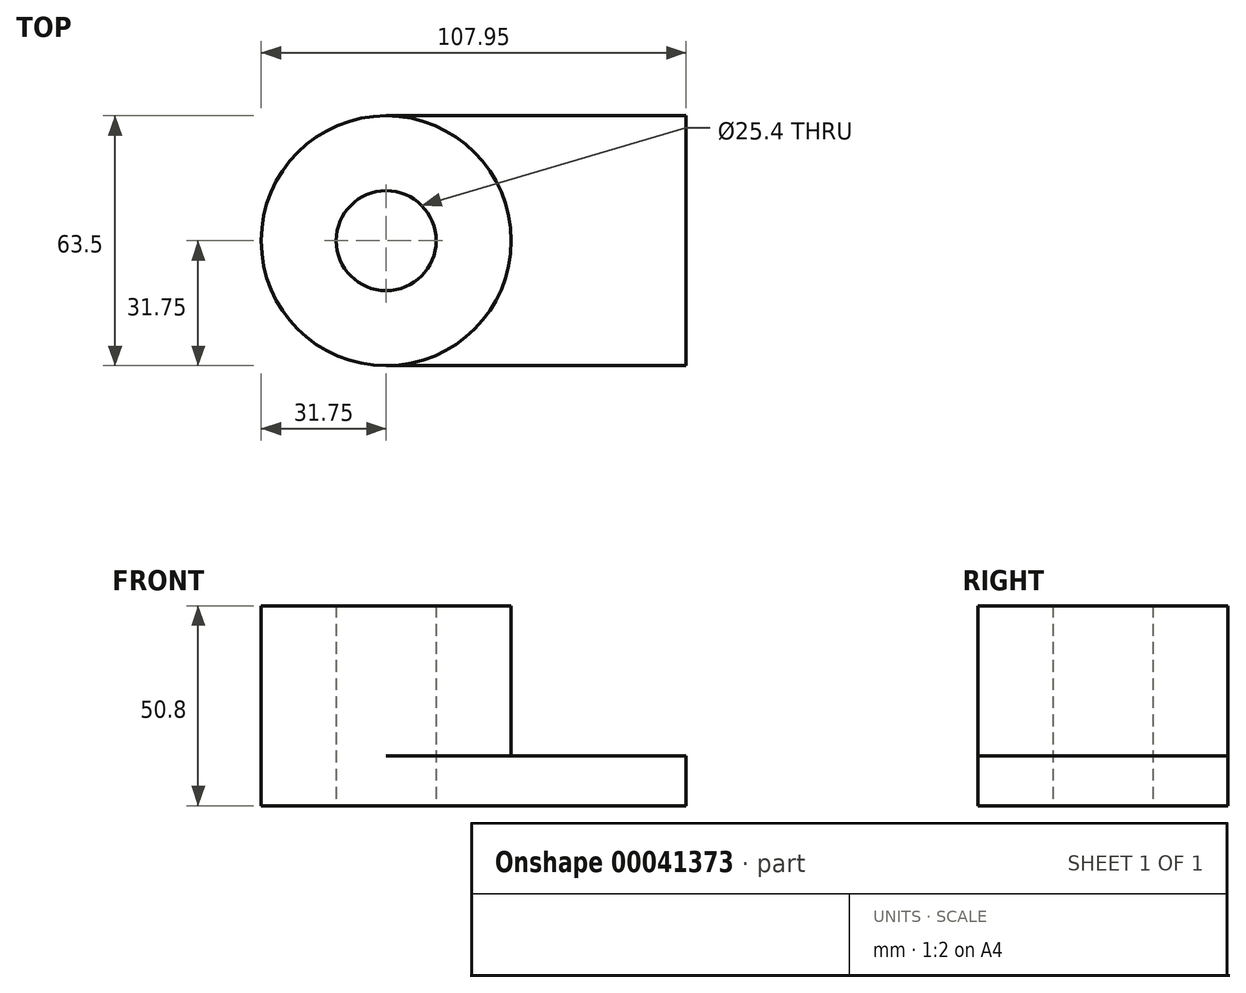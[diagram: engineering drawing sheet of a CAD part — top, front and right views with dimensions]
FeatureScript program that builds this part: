
annotation { "Feature Type Name" : "Feature", "Feature Type Description" : "" }
export const myFeature = defineFeature(function(context is Context, id is Id, definition is map)
    precondition{}
    {
        {
            var Q0;
            Q0=qCreatedBy(makeId("Top.planeOp"),FACE);
            var sketch = newSketch(context, id + "F0", { "sketchPlane" : qUnion([Q0])});
            skLineSegment(sketch, "E0.rect.bottom", {"start": v(38.1, -31.75) * mm, "end": v(-38.1, -31.75) * mm});
            skLineSegment(sketch, "E0.rect.top", {"start": v(38.1, 31.75) * mm, "end": v(-38.1, 31.75) * mm});
            skLineSegment(sketch, "E0.rect.left", {"start": v(38.1, -31.75) * mm, "end": v(38.1, 31.75) * mm});
            skLineSegment(sketch, "E0.rect.right", {"start": v(-38.1, -31.75) * mm, "end": v(-38.1, 31.75) * mm});
            skPoint(sketch, "E0.rect.middle", {"position": v(0, 0) * mm});
            skCircle(sketch, "E1", {"center": v(-38.1, 0) * mm, "radius": 31.75 * mm});
            skCircle(sketch, "E2", {"center": v(-38.1, 0) * mm, "radius": 12.7 * mm});
            skSolve(sketch);
        }
        {
            var Q0;
            {var subQ0=sQuery(id+"F0.wireOp",EDGE,"E2");var subQ1=sQuery(id+"F0.wireOp",EDGE,"E0.rect.right");var subQ3=makeQuery(id+"F0.imprint","INTERSECT",VERTEX,{"disambiguationData":[OD(0.0)],"derivedFrom":[subQ1,subQ0]});Q0=makeQuery(id+"F0.imprint","IMPRINT",FACE,{"disambiguationData":[TD([[makeQuery(id+"F0.imprint","IMPRINT",EDGE,{"disambiguationData":[TD([[subQ3,1.0]])],"derivedFrom":subQ0}),-1.0]])]});}
            var Q1;
            {var subQ0=sQuery(id+"F0.wireOp",EDGE,"E2");var subQ1=sQuery(id+"F0.wireOp",EDGE,"E0.rect.right");var subQ3=makeQuery(id+"F0.imprint","INTERSECT",VERTEX,{"disambiguationData":[OD(0.0)],"derivedFrom":[subQ1,subQ0]});Q1=makeQuery(id+"F0.imprint","IMPRINT",FACE,{"disambiguationData":[TD([[makeQuery(id+"F0.imprint","IMPRINT",EDGE,{"disambiguationData":[TD([[subQ3,-1.0]])],"derivedFrom":subQ0}),-1.0]])]});}
            var Q2;
            {var subQ3=sQuery(id+"F0.wireOp",EDGE,"E0.rect.bottom");Q2=makeQuery(id+"F0.imprint","IMPRINT",FACE,{"disambiguationData":[TD([[makeQuery(id+"F0.imprint","IMPRINT",EDGE,{"derivedFrom":subQ3}),-1.0]])]});}
            extrude(context, id + "F1", {"entities" : qUnion([Q0, Q1, Q2]), "depth" : 12.7 * mm});
        }
        {
            var Q0;
            {var subQ0=sQuery(id+"F0.wireOp",EDGE,"E2");var subQ1=sQuery(id+"F0.wireOp",EDGE,"E0.rect.right");var subQ3=makeQuery(id+"F0.imprint","INTERSECT",VERTEX,{"disambiguationData":[OD(0.0)],"derivedFrom":[subQ1,subQ0]});Q0=makeQuery(id+"F0.imprint","IMPRINT",FACE,{"disambiguationData":[TD([[makeQuery(id+"F0.imprint","IMPRINT",EDGE,{"disambiguationData":[TD([[subQ3,-1.0]])],"derivedFrom":subQ0}),-1.0]])]});}
            var Q1;
            {var subQ0=sQuery(id+"F0.wireOp",EDGE,"E2");var subQ1=sQuery(id+"F0.wireOp",EDGE,"E0.rect.right");var subQ3=makeQuery(id+"F0.imprint","INTERSECT",VERTEX,{"disambiguationData":[OD(0.0)],"derivedFrom":[subQ1,subQ0]});Q1=makeQuery(id+"F0.imprint","IMPRINT",FACE,{"disambiguationData":[TD([[makeQuery(id+"F0.imprint","IMPRINT",EDGE,{"disambiguationData":[TD([[subQ3,1.0]])],"derivedFrom":subQ0}),-1.0]])]});}
            extrude(context, id + "F2", {"entities" : qUnion([Q0, Q1]), "operationType" : NewBodyOperationType.ADD, "depth" : 50.8 * mm});
        }
    });
